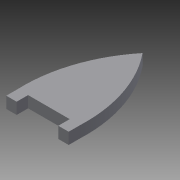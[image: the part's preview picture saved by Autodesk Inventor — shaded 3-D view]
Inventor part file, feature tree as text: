
AUTODESK INVENTOR PART (.ipt)
format: ipt  version: 2015 (Build 190159000, 159)  size: 77,312 bytes
history: native  units: mm
features: extrude x1, sketch x1
ambient origin geometry x8: Origin, YZ Plane, XZ Plane, XY Plane, X Axis, Y Axis, Z Axis, Center Point
bodies: Solid1 (feature_tree)
feature tree (2):
  extrude  "Extrusion1"  Depth=5.5mm
  sketch  "Sketch1"  dims[d0=15.0mm d1=5.5mm d2=5.0mm d3=5.5mm d4=0.0mm]
